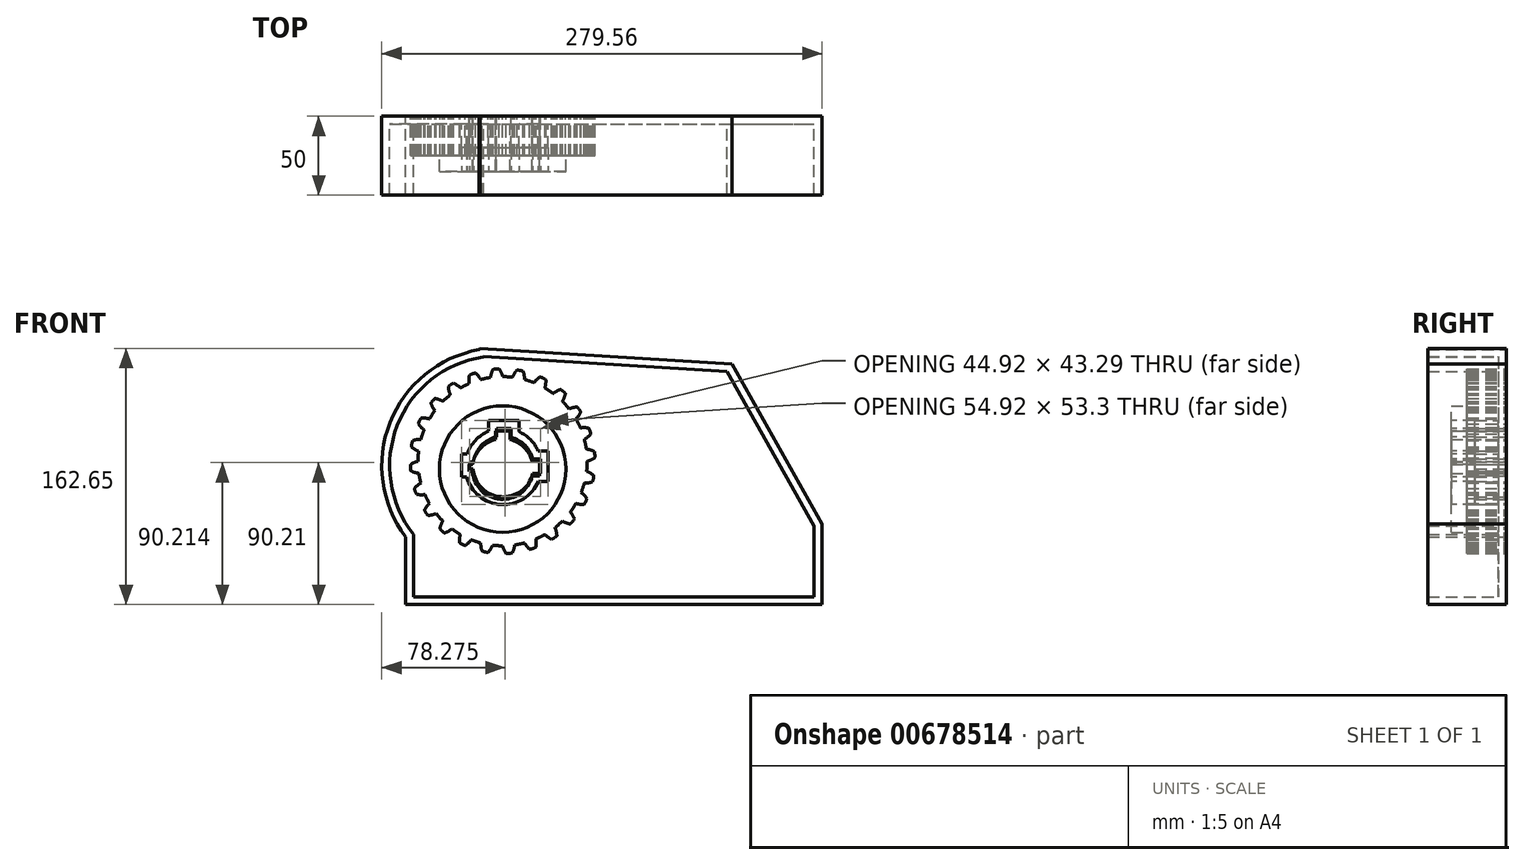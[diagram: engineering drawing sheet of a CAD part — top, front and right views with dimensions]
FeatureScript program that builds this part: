
annotation { "Feature Type Name" : "Feature", "Feature Type Description" : "" }
export const myFeature = defineFeature(function(context is Context, id is Id, definition is map)
    precondition{}
    {
        {
            var Q0;
            Q0=qCreatedBy(makeId("Front.planeOp"),FACE);
            var sketch = newSketch(context, id + "F0", { "sketchPlane" : qUnion([Q0])});
            skCircle(sketch, "E0", {"center": v(0, 4.95) * mm, "radius": 53.72 * mm});
            skCircle(sketch, "E1", {"center": v(0, 0) * mm, "radius": 58.67 * mm, "construction": true});
            skCircle(sketch, "E2", {"center": v(0, 0) * mm, "radius": 63.5 * mm, "construction": true});
            skLineSegment(sketch, "E3", {"start": v(0, 4.95) * mm, "end": v(0, 88.9) * mm, "construction": true});
            skLineSegment(sketch, "E4", {"start": v(0, 0) * mm, "end": v(-5.97, 91.1) * mm, "construction": true});
            skLineSegment(sketch, "E5", {"start": v(0, 58.67) * mm, "end": v(-58.6, 65.36) * mm, "construction": true});
            skLineSegment(sketch, "E6", {"start": v(0, 58.67) * mm, "end": v(-58.6, 44.62) * mm, "construction": true});
            skCircle(sketch, "E7", {"center": v(0, 4.95) * mm, "radius": 52.24 * mm, "construction": true});
            skCircle(sketch, "E8", {"center": v(0, 58.67) * mm, "radius": 14.6 * mm, "construction": true});
            skCircle(sketch, "E9", {"center": v(-14.2, 55.27) * mm, "radius": 14.6 * mm, "construction": true});
            skArc(sketch, "E10", {"start": v(0, 58.67) * mm, "mid": v(-0.85, 61.16) * mm, "end": v(-2.11, 63.46) * mm});
            skLineSegment(sketch, "E11", {"start": v(0, 58.67) * mm, "end": v(0, 58.67) * mm});
            skArc(sketch, "E12.MirrorCS", {"start": v(-7.66, 58.17) * mm, "mid": v(-7.14, 60.75) * mm, "end": v(-6.19, 63.2) * mm});
            skLineSegment(sketch, "E13.MirrorCS", {"start": v(-7.66, 58.17) * mm, "end": v(-7.66, 58.17) * mm});
            skArc(sketch, "E14", {"start": v(-2.11, 63.46) * mm, "mid": v(-4.16, 63.52) * mm, "end": v(-6.19, 63.2) * mm});
            skLineSegment(sketch, "E15", {"start": v(-7.66, 58.17) * mm, "end": v(-7.68, 58.12) * mm});
            skCircle(sketch, "E16", {"center": v(0, 0) * mm, "radius": 19.25 * mm});
            skCircle(sketch, "E17", {"center": v(0, 0) * mm, "radius": 40.16 * mm});
            skLineSegment(sketch, "E18.top", {"start": v(-4.38, 24.1) * mm, "end": v(4.66, 24.1) * mm});
            skLineSegment(sketch, "E18.left", {"start": v(-4.38, 18.75) * mm, "end": v(-4.38, 24.1) * mm});
            skLineSegment(sketch, "E18.right", {"start": v(4.66, 18.75) * mm, "end": v(4.66, 24.1) * mm});
            skLineSegment(sketch, "E19.bottom", {"start": v(18.64, 4.8) * mm, "end": v(23.58, 4.8) * mm});
            skLineSegment(sketch, "E19.top", {"start": v(18.64, -4.5) * mm, "end": v(23.58, -4.5) * mm});
            skLineSegment(sketch, "E19.right", {"start": v(23.58, 4.8) * mm, "end": v(23.58, -4.5) * mm});
            skLineSegment(sketch, "E20.bottom", {"start": v(-19.18, -1.64) * mm, "end": v(-21.34, -1.64) * mm});
            skLineSegment(sketch, "E20.top", {"start": v(-19.18, 2.88) * mm, "end": v(-21.34, 2.88) * mm});
            skLineSegment(sketch, "E20.right", {"start": v(-21.34, -1.64) * mm, "end": v(-21.34, 2.88) * mm});
            skLineSegment(sketch, "E21", {"start": v(4.66, 18.75) * mm, "end": v(4.66, 18.68) * mm});
            skLineSegment(sketch, "E22", {"start": v(-19.18, 2.88) * mm, "end": v(-19.03, 2.88) * mm});
            skSolve(sketch);
        }
        {
            var Q0;
            {var subQ0=sQuery(id+"F0.wireOp",EDGE,"E10");Q0=makeQuery(id+"F0.imprint","IMPRINT",FACE,{"disambiguationData":[TD([[makeQuery(id+"F0.imprint","IMPRINT",EDGE,{"derivedFrom":subQ0}),1.0]])]});}
            var Q1;
            Q1=makeQuery(id+"F0.imprint","IMPRINT",FACE,{"disambiguationData":[TD([[makeQuery(id+"F0.imprint","IMPRINT",EDGE,{"derivedFrom":sQuery(id+"F0.wireOp",EDGE,"E17")}),-1.0]])]});
            extrude(context, id + "F1", {"entities" : qUnion([Q0, Q1]), "depth" : 25 * mm, "offsetDistance" : 25 * mm});
        }
        {
            var Q0;
            Q0=makeQuery(id+"F1.opExtrude","SWEPT_BODY",BODY,{"disambiguationData":[OSD([sQuery(id+"F0.wireOp",EDGE,"E0"),sQuery(id+"F0.wireOp",EDGE,"E10"),sQuery(id+"F0.wireOp",EDGE,"E12.MirrorCS"),sQuery(id+"F0.wireOp",EDGE,"E14"),sQuery(id+"F0.wireOp",EDGE,"E15")])]});
            var Q1;
            Q1=makeQuery(id+"F1.opExtrude","SWEPT_FACE",FACE,{"disambiguationData":[OSD([sQuery(id+"F0.wireOp",EDGE,"E0")])]});
            circularPattern(context, id + "F2", {"entities" : qUnion([Q0]), "axis" : qUnion([Q1]), "angle" : 360 * degree, "instanceCount" : 24, "equalSpace" : true});
        }
        {
            var Q0;
            Q0=makeQuery(id+"F0.imprint","IMPRINT",FACE,{"disambiguationData":[TD([[makeQuery(id+"F0.imprint","IMPRINT",EDGE,{"derivedFrom":sQuery(id+"F0.wireOp",EDGE,"E17")}),1.0]])]});
            extrude(context, id + "F3", {"entities" : qUnion([Q0]), "operationType" : NewBodyOperationType.ADD, "depth" : 35 * mm, "offsetDistance" : 25 * mm});
        }
        {
            var Q0;
            Q0=qCreatedBy(makeId("Front.planeOp"),FACE);
            var sketch = newSketch(context, id + "F4", { "sketchPlane" : qUnion([Q0])});
            skLineSegment(sketch, "E23", {"start": v(-61.54, -43.12) * mm, "end": v(-61.54, -86.12) * mm});
            skLineSegment(sketch, "E24", {"start": v(-61.54, -86.12) * mm, "end": v(202.81, -86.12) * mm});
            skLineSegment(sketch, "E25", {"start": v(202.81, -86.12) * mm, "end": v(202.81, -34.87) * mm});
            skArc(sketch, "E26", {"start": v(-14.88, 75.8) * mm, "mid": v(-71.58, 29.43) * mm, "end": v(-61.54, -43.12) * mm});
            skLineSegment(sketch, "E27", {"start": v(-14.23, 76.53) * mm, "end": v(145.59, 66.8) * mm});
            skLineSegment(sketch, "E28", {"start": v(145.59, 66.8) * mm, "end": v(202.81, -34.87) * mm});
            skLineSegment(sketch, "E29", {"start": v(-14.88, 75.8) * mm, "end": v(-14.23, 76.53) * mm});
            skCircle(sketch, "E30", {"center": v(0.4, 1.64) * mm, "radius": 19.25 * mm});
            skLineSegment(sketch, "E31.top", {"start": v(-3.97, 25.74) * mm, "end": v(5.47, 25.74) * mm});
            skLineSegment(sketch, "E31.left", {"start": v(-3.97, 20.39) * mm, "end": v(-3.97, 25.74) * mm});
            skLineSegment(sketch, "E31.right", {"start": v(5.47, 20.21) * mm, "end": v(5.47, 25.74) * mm});
            skLineSegment(sketch, "E32.bottom", {"start": v(19.05, 6.44) * mm, "end": v(23.98, 6.44) * mm});
            skLineSegment(sketch, "E32.top", {"start": v(19.05, -2.86) * mm, "end": v(23.98, -2.86) * mm});
            skLineSegment(sketch, "E32.right", {"start": v(23.98, 6.44) * mm, "end": v(23.98, -2.86) * mm});
            skLineSegment(sketch, "E33.bottom", {"start": v(-18.77, 0) * mm, "end": v(-20.93, 0) * mm});
            skLineSegment(sketch, "E33.top", {"start": v(-18.62, 4.53) * mm, "end": v(-20.93, 4.53) * mm});
            skLineSegment(sketch, "E33.right", {"start": v(-20.93, 0) * mm, "end": v(-20.93, 4.53) * mm});
            skSolve(sketch);
        }
        {
            var Q0;
            Q0=makeQuery(id+"F4.imprint","IMPRINT",FACE,{"disambiguationData":[TD([[makeQuery(id+"F4.imprint","IMPRINT",EDGE,{"derivedFrom":sQuery(id+"F4.wireOp",EDGE,"E23")}),1.0]])]});
            extrude(context, id + "F5", {"entities" : qUnion([Q0]), "depth" : 50 * mm, "offsetDistance" : 25 * mm});
        }
        {
            var Q0;
            Q0=makeQuery(id+"F5.opExtrude","CAP_FACE",FACE,{"disambiguationData":[OSD([sQuery(id+"F4.wireOp",EDGE,"E23"),sQuery(id+"F4.wireOp",EDGE,"E24"),sQuery(id+"F4.wireOp",EDGE,"E25"),sQuery(id+"F4.wireOp",EDGE,"E26"),sQuery(id+"F4.wireOp",EDGE,"E27"),sQuery(id+"F4.wireOp",EDGE,"E28"),sQuery(id+"F4.wireOp",EDGE,"E29")])],"isStart":false});
            shell(context, id + "F6", {"entities" : qUnion([Q0]), "thickness" : 5 * mm});
        }
        {
            var Q0;
            {var subQ0=sQuery(id+"F4.wireOp",EDGE,"E33.right");var subQ1=sQuery(id+"F4.wireOp",EDGE,"E33.top");var subQ2=sQuery(id+"F4.wireOp",EDGE,"E33.bottom");var subQ3=sQuery(id+"F4.wireOp",EDGE,"E32.right");var subQ4=sQuery(id+"F4.wireOp",EDGE,"E32.top");var subQ5=sQuery(id+"F4.wireOp",EDGE,"E32.bottom");var subQ6=sQuery(id+"F4.wireOp",EDGE,"E31.right");var subQ7=sQuery(id+"F4.wireOp",EDGE,"E31.left");var subQ8=sQuery(id+"F4.wireOp",EDGE,"E31.top");var subQ9=sQuery(id+"F4.wireOp",EDGE,"E30");var subQ10=sQuery(id+"F4.wireOp",EDGE,"E29");var subQ11=sQuery(id+"F4.wireOp",EDGE,"E28");var subQ12=sQuery(id+"F4.wireOp",EDGE,"E27");var subQ13=sQuery(id+"F4.wireOp",EDGE,"E26");var subQ14=sQuery(id+"F4.wireOp",EDGE,"E25");var subQ15=sQuery(id+"F4.wireOp",EDGE,"E24");var subQ16=sQuery(id+"F4.wireOp",EDGE,"E23");Q0=makeQuery(id+"F6.opShell","OFFSET_FACE",FACE,{"disambiguationData":[OSD([subQ16,subQ15,subQ14,subQ13,subQ12,subQ11,subQ10,subQ9,subQ8,subQ7,subQ6,subQ5,subQ4,subQ3,subQ2,subQ1,subQ0]),TDD([makeQuery(id+"F5.opExtrude","CAP_FACE",FACE,{"disambiguationData":[OSD([subQ16,subQ15,subQ14,subQ13,subQ12,subQ11,subQ10,subQ9,subQ8,subQ7,subQ6,subQ5,subQ4,subQ3,subQ2,subQ1,subQ0])],"isStart":false})])]});}
            extrude(context, id + "F7", {"entities" : qUnion([Q0]), "operationType" : NewBodyOperationType.REMOVE, "oppositeDirection" : true, "depth" : 30 * mm, "offsetDistance" : 25 * mm});
        }
    });
